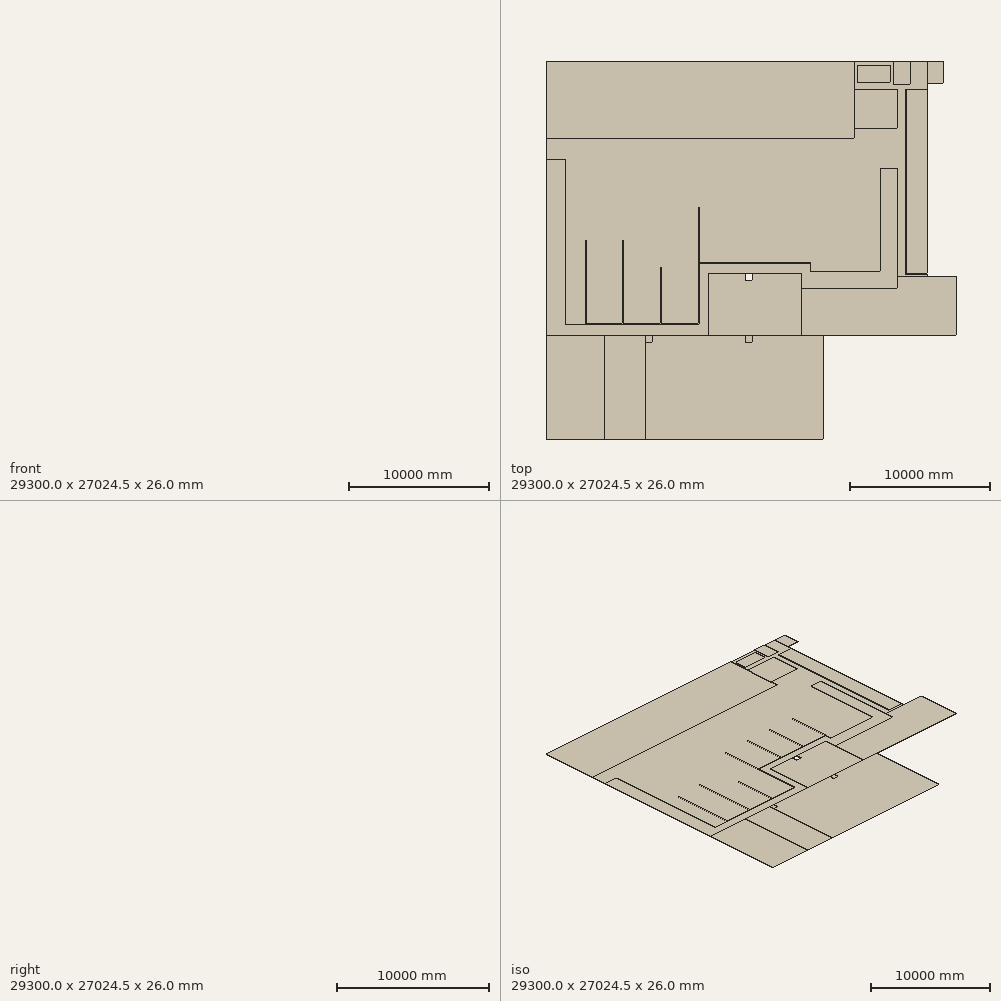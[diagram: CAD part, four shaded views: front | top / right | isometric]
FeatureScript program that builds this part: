
annotation { "Feature Type Name" : "Feature", "Feature Type Description" : "" }
export const myFeature = defineFeature(function(context is Context, id is Id, definition is map)
    precondition{}
    {
        {
            var Q0;
            Q0=qCreatedBy(makeId("Top.planeOp"),FACE);
            var sketch = newSketch(context, id + "F0", { "sketchPlane" : qUnion([Q0])});
            skLineSegment(sketch, "E0", {"start": v(10928.58, -1480) * mm, "end": v(12438.58, -1480) * mm});
            skLineSegment(sketch, "E1", {"start": v(12438.58, 11730) * mm, "end": v(10928.58, 11730) * mm});
            skLineSegment(sketch, "E2", {"start": v(10928.58, 11730) * mm, "end": v(10928.58, -1480) * mm});
            skLineSegment(sketch, "E3", {"start": v(10938.58, 11720) * mm, "end": v(10938.58, -1470) * mm});
            skLineSegment(sketch, "E4", {"start": v(12438.58, 11720) * mm, "end": v(10938.58, 11720) * mm});
            skLineSegment(sketch, "E5", {"start": v(10938.58, -1470) * mm, "end": v(12438.58, -1470) * mm});
            skLineSegment(sketch, "E6", {"start": v(12438.58, -1470) * mm, "end": v(12438.58, -1480) * mm});
            skLineSegment(sketch, "E7", {"start": v(12438.58, 11730) * mm, "end": v(12438.58, 11720) * mm});
            skLineSegment(sketch, "E8", {"start": v(13638.58, 12120) * mm, "end": v(13638.58, 13720) * mm});
            skLineSegment(sketch, "E9", {"start": v(12438.58, 12120) * mm, "end": v(13638.58, 12120) * mm});
            skLineSegment(sketch, "E10", {"start": v(12438.58, 11730) * mm, "end": v(12438.58, 12120) * mm});
            skLineSegment(sketch, "E11", {"start": v(-14761.42, -5870) * mm, "end": v(-14761.42, -13304.54) * mm});
            skLineSegment(sketch, "E12", {"start": v(-14761.42, -13304.54) * mm, "end": v(5038.58, -13304.54) * mm});
            skLineSegment(sketch, "E13", {"start": v(5038.58, -13304.54) * mm, "end": v(5038.58, -5870) * mm});
            skLineSegment(sketch, "E14", {"start": v(12438.58, -1670) * mm, "end": v(14538.58, -1670) * mm});
            skLineSegment(sketch, "E15", {"start": v(14538.58, -1670) * mm, "end": v(14538.58, -5870) * mm});
            skLineSegment(sketch, "E16", {"start": v(14538.58, -5870) * mm, "end": v(5038.58, -5870) * mm});
            skLineSegment(sketch, "E17", {"start": v(12438.58, -1480) * mm, "end": v(12438.58, -1670) * mm});
            skLineSegment(sketch, "E18", {"start": v(13638.58, 13720) * mm, "end": v(13542.58, 13720) * mm});
            skLineSegment(sketch, "E19", {"start": v(13542.58, 13720) * mm, "end": v(13540.58, 13718) * mm});
            skLineSegment(sketch, "E20", {"start": v(13540.58, 13718) * mm, "end": v(13440.58, 13718) * mm});
            skLineSegment(sketch, "E21", {"start": v(13440.58, 13718) * mm, "end": v(13438.58, 13720) * mm});
            skLineSegment(sketch, "E22", {"start": v(13438.58, 13720) * mm, "end": v(13142.58, 13720) * mm});
            skLineSegment(sketch, "E23", {"start": v(13142.58, 13720) * mm, "end": v(13140.58, 13718) * mm});
            skLineSegment(sketch, "E24", {"start": v(13140.58, 13718) * mm, "end": v(13040.58, 13718) * mm});
            skLineSegment(sketch, "E25", {"start": v(13040.58, 13718) * mm, "end": v(13038.58, 13720) * mm});
            skLineSegment(sketch, "E26", {"start": v(13038.58, 13720) * mm, "end": v(12742.58, 13720) * mm});
            skLineSegment(sketch, "E27", {"start": v(12742.58, 13720) * mm, "end": v(12740.58, 13718) * mm});
            skLineSegment(sketch, "E28", {"start": v(12740.58, 13718) * mm, "end": v(12640.58, 13718) * mm});
            skLineSegment(sketch, "E29", {"start": v(12640.58, 13718) * mm, "end": v(12638.58, 13720) * mm});
            skLineSegment(sketch, "E30", {"start": v(12638.58, 13720) * mm, "end": v(12342.58, 13720) * mm});
            skLineSegment(sketch, "E31", {"start": v(12342.58, 13720) * mm, "end": v(12340.58, 13718) * mm});
            skLineSegment(sketch, "E32", {"start": v(12340.58, 13718) * mm, "end": v(12240.58, 13718) * mm});
            skLineSegment(sketch, "E33", {"start": v(12240.58, 13718) * mm, "end": v(12238.58, 13720) * mm});
            skLineSegment(sketch, "E34", {"start": v(12238.58, 13720) * mm, "end": v(11942.58, 13720) * mm});
            skLineSegment(sketch, "E35", {"start": v(11942.58, 13720) * mm, "end": v(11940.58, 13718) * mm});
            skLineSegment(sketch, "E36", {"start": v(11940.58, 13718) * mm, "end": v(11840.58, 13718) * mm});
            skLineSegment(sketch, "E37", {"start": v(11840.58, 13718) * mm, "end": v(11838.58, 13720) * mm});
            skLineSegment(sketch, "E38", {"start": v(11838.58, 13720) * mm, "end": v(11542.58, 13720) * mm});
            skLineSegment(sketch, "E39", {"start": v(11542.58, 13720) * mm, "end": v(11540.58, 13718) * mm});
            skLineSegment(sketch, "E40", {"start": v(11540.58, 13718) * mm, "end": v(11440.58, 13718) * mm});
            skLineSegment(sketch, "E41", {"start": v(11440.58, 13718) * mm, "end": v(11438.58, 13720) * mm});
            skLineSegment(sketch, "E42", {"start": v(11438.58, 13720) * mm, "end": v(11142.58, 13720) * mm});
            skLineSegment(sketch, "E43", {"start": v(11142.58, 13720) * mm, "end": v(11140.58, 13718) * mm});
            skLineSegment(sketch, "E44", {"start": v(11140.58, 13718) * mm, "end": v(11040.58, 13718) * mm});
            skLineSegment(sketch, "E45", {"start": v(11040.58, 13718) * mm, "end": v(11038.58, 13720) * mm});
            skLineSegment(sketch, "E46", {"start": v(11038.58, 13720) * mm, "end": v(10742.58, 13720) * mm});
            skLineSegment(sketch, "E47", {"start": v(10742.58, 13720) * mm, "end": v(10740.58, 13718) * mm});
            skLineSegment(sketch, "E48", {"start": v(10740.58, 13718) * mm, "end": v(10640.58, 13718) * mm});
            skLineSegment(sketch, "E49", {"start": v(10640.58, 13718) * mm, "end": v(10638.58, 13720) * mm});
            skLineSegment(sketch, "E50", {"start": v(10638.58, 13720) * mm, "end": v(10342.58, 13720) * mm});
            skLineSegment(sketch, "E51", {"start": v(10342.58, 13720) * mm, "end": v(10340.58, 13718) * mm});
            skLineSegment(sketch, "E52", {"start": v(10340.58, 13718) * mm, "end": v(10240.58, 13718) * mm});
            skLineSegment(sketch, "E53", {"start": v(10240.58, 13718) * mm, "end": v(10238.58, 13720) * mm});
            skLineSegment(sketch, "E54", {"start": v(10238.58, 13720) * mm, "end": v(9942.58, 13720) * mm});
            skLineSegment(sketch, "E55", {"start": v(9942.58, 13720) * mm, "end": v(9940.58, 13718) * mm});
            skLineSegment(sketch, "E56", {"start": v(9940.58, 13718) * mm, "end": v(9840.58, 13718) * mm});
            skLineSegment(sketch, "E57", {"start": v(9840.58, 13718) * mm, "end": v(9838.58, 13720) * mm});
            skLineSegment(sketch, "E58", {"start": v(9838.58, 13720) * mm, "end": v(9542.58, 13720) * mm});
            skLineSegment(sketch, "E59", {"start": v(9542.58, 13720) * mm, "end": v(9540.58, 13718) * mm});
            skLineSegment(sketch, "E60", {"start": v(9540.58, 13718) * mm, "end": v(9440.58, 13718) * mm});
            skLineSegment(sketch, "E61", {"start": v(9440.58, 13718) * mm, "end": v(9438.58, 13720) * mm});
            skLineSegment(sketch, "E62", {"start": v(9438.58, 13720) * mm, "end": v(9142.58, 13720) * mm});
            skLineSegment(sketch, "E63", {"start": v(9142.58, 13720) * mm, "end": v(9140.58, 13718) * mm});
            skLineSegment(sketch, "E64", {"start": v(9140.58, 13718) * mm, "end": v(9040.58, 13718) * mm});
            skLineSegment(sketch, "E65", {"start": v(9040.58, 13718) * mm, "end": v(9038.58, 13720) * mm});
            skLineSegment(sketch, "E66", {"start": v(9038.58, 13720) * mm, "end": v(8742.58, 13720) * mm});
            skLineSegment(sketch, "E67", {"start": v(8742.58, 13720) * mm, "end": v(8740.58, 13718) * mm});
            skLineSegment(sketch, "E68", {"start": v(8740.58, 13718) * mm, "end": v(8640.58, 13718) * mm});
            skLineSegment(sketch, "E69", {"start": v(8640.58, 13718) * mm, "end": v(8638.58, 13720) * mm});
            skLineSegment(sketch, "E70", {"start": v(8638.58, 13720) * mm, "end": v(8342.58, 13720) * mm});
            skLineSegment(sketch, "E71", {"start": v(8342.58, 13720) * mm, "end": v(8340.58, 13718) * mm});
            skLineSegment(sketch, "E72", {"start": v(8340.58, 13718) * mm, "end": v(8240.58, 13718) * mm});
            skLineSegment(sketch, "E73", {"start": v(8240.58, 13718) * mm, "end": v(8238.58, 13720) * mm});
            skLineSegment(sketch, "E74", {"start": v(8238.58, 13720) * mm, "end": v(7942.58, 13720) * mm});
            skLineSegment(sketch, "E75", {"start": v(7942.58, 13720) * mm, "end": v(7940.58, 13718) * mm});
            skLineSegment(sketch, "E76", {"start": v(7940.58, 13718) * mm, "end": v(7840.58, 13718) * mm});
            skLineSegment(sketch, "E77", {"start": v(7840.58, 13718) * mm, "end": v(7838.58, 13720) * mm});
            skLineSegment(sketch, "E78", {"start": v(7838.58, 13720) * mm, "end": v(7542.58, 13720) * mm});
            skLineSegment(sketch, "E79", {"start": v(7542.58, 13720) * mm, "end": v(7540.58, 13718) * mm});
            skLineSegment(sketch, "E80", {"start": v(7540.58, 13718) * mm, "end": v(7440.58, 13718) * mm});
            skLineSegment(sketch, "E81", {"start": v(7440.58, 13718) * mm, "end": v(7438.58, 13720) * mm});
            skLineSegment(sketch, "E82", {"start": v(7438.58, 13720) * mm, "end": v(7142.58, 13720) * mm});
            skLineSegment(sketch, "E83", {"start": v(7142.58, 13720) * mm, "end": v(7140.58, 13718) * mm});
            skLineSegment(sketch, "E84", {"start": v(7140.58, 13718) * mm, "end": v(7040.58, 13718) * mm});
            skLineSegment(sketch, "E85", {"start": v(7040.58, 13718) * mm, "end": v(7038.58, 13720) * mm});
            skLineSegment(sketch, "E86", {"start": v(7038.58, 13720) * mm, "end": v(6742.58, 13720) * mm});
            skLineSegment(sketch, "E87", {"start": v(6742.58, 13720) * mm, "end": v(6740.58, 13718) * mm});
            skLineSegment(sketch, "E88", {"start": v(6740.58, 13718) * mm, "end": v(6640.58, 13718) * mm});
            skLineSegment(sketch, "E89", {"start": v(6640.58, 13718) * mm, "end": v(6638.58, 13720) * mm});
            skLineSegment(sketch, "E90", {"start": v(6638.58, 13720) * mm, "end": v(6342.58, 13720) * mm});
            skLineSegment(sketch, "E91", {"start": v(6342.58, 13720) * mm, "end": v(6340.58, 13718) * mm});
            skLineSegment(sketch, "E92", {"start": v(6340.58, 13718) * mm, "end": v(6240.58, 13718) * mm});
            skLineSegment(sketch, "E93", {"start": v(6240.58, 13718) * mm, "end": v(6238.58, 13720) * mm});
            skLineSegment(sketch, "E94", {"start": v(6238.58, 13720) * mm, "end": v(5942.58, 13720) * mm});
            skLineSegment(sketch, "E95", {"start": v(5942.58, 13720) * mm, "end": v(5940.58, 13718) * mm});
            skLineSegment(sketch, "E96", {"start": v(5940.58, 13718) * mm, "end": v(5840.58, 13718) * mm});
            skLineSegment(sketch, "E97", {"start": v(5840.58, 13718) * mm, "end": v(5838.58, 13720) * mm});
            skLineSegment(sketch, "E98", {"start": v(5838.58, 13720) * mm, "end": v(5542.58, 13720) * mm});
            skLineSegment(sketch, "E99", {"start": v(5542.58, 13720) * mm, "end": v(5540.58, 13718) * mm});
            skLineSegment(sketch, "E100", {"start": v(5540.58, 13718) * mm, "end": v(5440.58, 13718) * mm});
            skLineSegment(sketch, "E101", {"start": v(5440.58, 13718) * mm, "end": v(5438.58, 13720) * mm});
            skLineSegment(sketch, "E102", {"start": v(5438.58, 13720) * mm, "end": v(5142.58, 13720) * mm});
            skLineSegment(sketch, "E103", {"start": v(5142.58, 13720) * mm, "end": v(5140.58, 13718) * mm});
            skLineSegment(sketch, "E104", {"start": v(5140.58, 13718) * mm, "end": v(5040.58, 13718) * mm});
            skLineSegment(sketch, "E105", {"start": v(5040.58, 13718) * mm, "end": v(5038.58, 13720) * mm});
            skLineSegment(sketch, "E106", {"start": v(5038.58, 13720) * mm, "end": v(4742.58, 13720) * mm});
            skLineSegment(sketch, "E107", {"start": v(4742.58, 13720) * mm, "end": v(4740.58, 13718) * mm});
            skLineSegment(sketch, "E108", {"start": v(4740.58, 13718) * mm, "end": v(4640.58, 13718) * mm});
            skLineSegment(sketch, "E109", {"start": v(4640.58, 13718) * mm, "end": v(4638.58, 13720) * mm});
            skLineSegment(sketch, "E110", {"start": v(4638.58, 13720) * mm, "end": v(4342.58, 13720) * mm});
            skLineSegment(sketch, "E111", {"start": v(4342.58, 13720) * mm, "end": v(4340.58, 13718) * mm});
            skLineSegment(sketch, "E112", {"start": v(4340.58, 13718) * mm, "end": v(4240.58, 13718) * mm});
            skLineSegment(sketch, "E113", {"start": v(4240.58, 13718) * mm, "end": v(4238.58, 13720) * mm});
            skLineSegment(sketch, "E114", {"start": v(4238.58, 13720) * mm, "end": v(3942.58, 13720) * mm});
            skLineSegment(sketch, "E115", {"start": v(3942.58, 13720) * mm, "end": v(3940.58, 13718) * mm});
            skLineSegment(sketch, "E116", {"start": v(3940.58, 13718) * mm, "end": v(3840.58, 13718) * mm});
            skLineSegment(sketch, "E117", {"start": v(3840.58, 13718) * mm, "end": v(3838.58, 13720) * mm});
            skLineSegment(sketch, "E118", {"start": v(3838.58, 13720) * mm, "end": v(3542.58, 13720) * mm});
            skLineSegment(sketch, "E119", {"start": v(3542.58, 13720) * mm, "end": v(3540.58, 13718) * mm});
            skLineSegment(sketch, "E120", {"start": v(3540.58, 13718) * mm, "end": v(3440.58, 13718) * mm});
            skLineSegment(sketch, "E121", {"start": v(3440.58, 13718) * mm, "end": v(3438.58, 13720) * mm});
            skLineSegment(sketch, "E122", {"start": v(3438.58, 13720) * mm, "end": v(3142.58, 13720) * mm});
            skLineSegment(sketch, "E123", {"start": v(3142.58, 13720) * mm, "end": v(3140.58, 13718) * mm});
            skLineSegment(sketch, "E124", {"start": v(3140.58, 13718) * mm, "end": v(3040.58, 13718) * mm});
            skLineSegment(sketch, "E125", {"start": v(3040.58, 13718) * mm, "end": v(3038.58, 13720) * mm});
            skLineSegment(sketch, "E126", {"start": v(3038.58, 13720) * mm, "end": v(2742.58, 13720) * mm});
            skLineSegment(sketch, "E127", {"start": v(2742.58, 13720) * mm, "end": v(2740.58, 13718) * mm});
            skLineSegment(sketch, "E128", {"start": v(2740.58, 13718) * mm, "end": v(2640.58, 13718) * mm});
            skLineSegment(sketch, "E129", {"start": v(2640.58, 13718) * mm, "end": v(2638.58, 13720) * mm});
            skLineSegment(sketch, "E130", {"start": v(2638.58, 13720) * mm, "end": v(2342.58, 13720) * mm});
            skLineSegment(sketch, "E131", {"start": v(2342.58, 13720) * mm, "end": v(2340.58, 13718) * mm});
            skLineSegment(sketch, "E132", {"start": v(2340.58, 13718) * mm, "end": v(2240.58, 13718) * mm});
            skLineSegment(sketch, "E133", {"start": v(2240.58, 13718) * mm, "end": v(2238.58, 13720) * mm});
            skLineSegment(sketch, "E134", {"start": v(2238.58, 13720) * mm, "end": v(1942.58, 13720) * mm});
            skLineSegment(sketch, "E135", {"start": v(1942.58, 13720) * mm, "end": v(1940.58, 13718) * mm});
            skLineSegment(sketch, "E136", {"start": v(1940.58, 13718) * mm, "end": v(1840.58, 13718) * mm});
            skLineSegment(sketch, "E137", {"start": v(1840.58, 13718) * mm, "end": v(1838.58, 13720) * mm});
            skLineSegment(sketch, "E138", {"start": v(1838.58, 13720) * mm, "end": v(1542.58, 13720) * mm});
            skLineSegment(sketch, "E139", {"start": v(1542.58, 13720) * mm, "end": v(1540.58, 13718) * mm});
            skLineSegment(sketch, "E140", {"start": v(1540.58, 13718) * mm, "end": v(1440.58, 13718) * mm});
            skLineSegment(sketch, "E141", {"start": v(1440.58, 13718) * mm, "end": v(1438.58, 13720) * mm});
            skLineSegment(sketch, "E142", {"start": v(1438.58, 13720) * mm, "end": v(1142.58, 13720) * mm});
            skLineSegment(sketch, "E143", {"start": v(1142.58, 13720) * mm, "end": v(1140.58, 13718) * mm});
            skLineSegment(sketch, "E144", {"start": v(1140.58, 13718) * mm, "end": v(1040.58, 13718) * mm});
            skLineSegment(sketch, "E145", {"start": v(1040.58, 13718) * mm, "end": v(1038.58, 13720) * mm});
            skLineSegment(sketch, "E146", {"start": v(1038.58, 13720) * mm, "end": v(742.58, 13720) * mm});
            skLineSegment(sketch, "E147", {"start": v(742.58, 13720) * mm, "end": v(740.58, 13718) * mm});
            skLineSegment(sketch, "E148", {"start": v(740.58, 13718) * mm, "end": v(640.58, 13718) * mm});
            skLineSegment(sketch, "E149", {"start": v(640.58, 13718) * mm, "end": v(638.58, 13720) * mm});
            skLineSegment(sketch, "E150", {"start": v(638.58, 13720) * mm, "end": v(342.58, 13720) * mm});
            skLineSegment(sketch, "E151", {"start": v(342.58, 13720) * mm, "end": v(340.58, 13718) * mm});
            skLineSegment(sketch, "E152", {"start": v(340.58, 13718) * mm, "end": v(240.58, 13718) * mm});
            skLineSegment(sketch, "E153", {"start": v(240.58, 13718) * mm, "end": v(238.58, 13720) * mm});
            skLineSegment(sketch, "E154", {"start": v(238.58, 13720) * mm, "end": v(-57.42, 13720) * mm});
            skLineSegment(sketch, "E155", {"start": v(-57.42, 13720) * mm, "end": v(-59.42, 13718) * mm});
            skLineSegment(sketch, "E156", {"start": v(-59.42, 13718) * mm, "end": v(-159.42, 13718) * mm});
            skLineSegment(sketch, "E157", {"start": v(-159.42, 13718) * mm, "end": v(-161.42, 13720) * mm});
            skLineSegment(sketch, "E158", {"start": v(-161.42, 13720) * mm, "end": v(-457.42, 13720) * mm});
            skLineSegment(sketch, "E159", {"start": v(-457.42, 13720) * mm, "end": v(-459.42, 13718) * mm});
            skLineSegment(sketch, "E160", {"start": v(-459.42, 13718) * mm, "end": v(-559.42, 13718) * mm});
            skLineSegment(sketch, "E161", {"start": v(-559.42, 13718) * mm, "end": v(-561.42, 13720) * mm});
            skLineSegment(sketch, "E162", {"start": v(-561.42, 13720) * mm, "end": v(-857.42, 13720) * mm});
            skLineSegment(sketch, "E163", {"start": v(-857.42, 13720) * mm, "end": v(-859.42, 13718) * mm});
            skLineSegment(sketch, "E164", {"start": v(-859.42, 13718) * mm, "end": v(-959.42, 13718) * mm});
            skLineSegment(sketch, "E165", {"start": v(-959.42, 13718) * mm, "end": v(-961.42, 13720) * mm});
            skLineSegment(sketch, "E166", {"start": v(-961.42, 13720) * mm, "end": v(-1257.42, 13720) * mm});
            skLineSegment(sketch, "E167", {"start": v(-1257.42, 13720) * mm, "end": v(-1259.42, 13718) * mm});
            skLineSegment(sketch, "E168", {"start": v(-1259.42, 13718) * mm, "end": v(-1359.42, 13718) * mm});
            skLineSegment(sketch, "E169", {"start": v(-1359.42, 13718) * mm, "end": v(-1361.42, 13720) * mm});
            skLineSegment(sketch, "E170", {"start": v(-1361.42, 13720) * mm, "end": v(-1657.42, 13720) * mm});
            skLineSegment(sketch, "E171", {"start": v(-1657.42, 13720) * mm, "end": v(-1659.42, 13718) * mm});
            skLineSegment(sketch, "E172", {"start": v(-1659.42, 13718) * mm, "end": v(-1759.42, 13718) * mm});
            skLineSegment(sketch, "E173", {"start": v(-1759.42, 13718) * mm, "end": v(-1761.42, 13720) * mm});
            skLineSegment(sketch, "E174", {"start": v(-1761.42, 13720) * mm, "end": v(-2057.42, 13720) * mm});
            skLineSegment(sketch, "E175", {"start": v(-2057.42, 13720) * mm, "end": v(-2059.42, 13718) * mm});
            skLineSegment(sketch, "E176", {"start": v(-2059.42, 13718) * mm, "end": v(-2159.42, 13718) * mm});
            skLineSegment(sketch, "E177", {"start": v(-2159.42, 13718) * mm, "end": v(-2161.42, 13720) * mm});
            skLineSegment(sketch, "E178", {"start": v(-2161.42, 13720) * mm, "end": v(-2457.42, 13720) * mm});
            skLineSegment(sketch, "E179", {"start": v(-2457.42, 13720) * mm, "end": v(-2459.42, 13718) * mm});
            skLineSegment(sketch, "E180", {"start": v(-2459.42, 13718) * mm, "end": v(-2559.42, 13718) * mm});
            skLineSegment(sketch, "E181", {"start": v(-2559.42, 13718) * mm, "end": v(-2561.42, 13720) * mm});
            skLineSegment(sketch, "E182", {"start": v(-2561.42, 13720) * mm, "end": v(-2857.42, 13720) * mm});
            skLineSegment(sketch, "E183", {"start": v(-2857.42, 13720) * mm, "end": v(-2859.42, 13718) * mm});
            skLineSegment(sketch, "E184", {"start": v(-2859.42, 13718) * mm, "end": v(-2959.42, 13718) * mm});
            skLineSegment(sketch, "E185", {"start": v(-2959.42, 13718) * mm, "end": v(-2961.42, 13720) * mm});
            skLineSegment(sketch, "E186", {"start": v(-2961.42, 13720) * mm, "end": v(-3257.42, 13720) * mm});
            skLineSegment(sketch, "E187", {"start": v(-3257.42, 13720) * mm, "end": v(-3259.42, 13718) * mm});
            skLineSegment(sketch, "E188", {"start": v(-3259.42, 13718) * mm, "end": v(-3359.42, 13718) * mm});
            skLineSegment(sketch, "E189", {"start": v(-3359.42, 13718) * mm, "end": v(-3361.42, 13720) * mm});
            skLineSegment(sketch, "E190", {"start": v(-3361.42, 13720) * mm, "end": v(-3657.42, 13720) * mm});
            skLineSegment(sketch, "E191", {"start": v(-3657.42, 13720) * mm, "end": v(-3659.42, 13718) * mm});
            skLineSegment(sketch, "E192", {"start": v(-3659.42, 13718) * mm, "end": v(-3759.42, 13718) * mm});
            skLineSegment(sketch, "E193", {"start": v(-3759.42, 13718) * mm, "end": v(-3761.42, 13720) * mm});
            skLineSegment(sketch, "E194", {"start": v(-3761.42, 13720) * mm, "end": v(-4057.42, 13720) * mm});
            skLineSegment(sketch, "E195", {"start": v(-4057.42, 13720) * mm, "end": v(-4059.42, 13718) * mm});
            skLineSegment(sketch, "E196", {"start": v(-4059.42, 13718) * mm, "end": v(-4159.42, 13718) * mm});
            skLineSegment(sketch, "E197", {"start": v(-4159.42, 13718) * mm, "end": v(-4161.42, 13720) * mm});
            skLineSegment(sketch, "E198", {"start": v(-4161.42, 13720) * mm, "end": v(-4457.42, 13720) * mm});
            skLineSegment(sketch, "E199", {"start": v(-4457.42, 13720) * mm, "end": v(-4459.42, 13718) * mm});
            skLineSegment(sketch, "E200", {"start": v(-4459.42, 13718) * mm, "end": v(-4559.42, 13718) * mm});
            skLineSegment(sketch, "E201", {"start": v(-4559.42, 13718) * mm, "end": v(-4561.42, 13720) * mm});
            skLineSegment(sketch, "E202", {"start": v(-4561.42, 13720) * mm, "end": v(-4857.42, 13720) * mm});
            skLineSegment(sketch, "E203", {"start": v(-4857.42, 13720) * mm, "end": v(-4859.42, 13718) * mm});
            skLineSegment(sketch, "E204", {"start": v(-4859.42, 13718) * mm, "end": v(-4959.42, 13718) * mm});
            skLineSegment(sketch, "E205", {"start": v(-4959.42, 13718) * mm, "end": v(-4961.42, 13720) * mm});
            skLineSegment(sketch, "E206", {"start": v(-4961.42, 13720) * mm, "end": v(-5257.42, 13720) * mm});
            skLineSegment(sketch, "E207", {"start": v(-5257.42, 13720) * mm, "end": v(-5259.42, 13718) * mm});
            skLineSegment(sketch, "E208", {"start": v(-5259.42, 13718) * mm, "end": v(-5359.42, 13718) * mm});
            skLineSegment(sketch, "E209", {"start": v(-5359.42, 13718) * mm, "end": v(-5361.42, 13720) * mm});
            skLineSegment(sketch, "E210", {"start": v(-5361.42, 13720) * mm, "end": v(-5657.42, 13720) * mm});
            skLineSegment(sketch, "E211", {"start": v(-5657.42, 13720) * mm, "end": v(-5659.42, 13718) * mm});
            skLineSegment(sketch, "E212", {"start": v(-5659.42, 13718) * mm, "end": v(-5759.42, 13718) * mm});
            skLineSegment(sketch, "E213", {"start": v(-5759.42, 13718) * mm, "end": v(-5761.42, 13720) * mm});
            skLineSegment(sketch, "E214", {"start": v(-5761.42, 13720) * mm, "end": v(-6057.42, 13720) * mm});
            skLineSegment(sketch, "E215", {"start": v(-6057.42, 13720) * mm, "end": v(-6059.42, 13718) * mm});
            skLineSegment(sketch, "E216", {"start": v(-6059.42, 13718) * mm, "end": v(-6159.42, 13718) * mm});
            skLineSegment(sketch, "E217", {"start": v(-6159.42, 13718) * mm, "end": v(-6161.42, 13720) * mm});
            skLineSegment(sketch, "E218", {"start": v(-6161.42, 13720) * mm, "end": v(-6457.42, 13720) * mm});
            skLineSegment(sketch, "E219", {"start": v(-6457.42, 13720) * mm, "end": v(-6459.42, 13718) * mm});
            skLineSegment(sketch, "E220", {"start": v(-6459.42, 13718) * mm, "end": v(-6559.42, 13718) * mm});
            skLineSegment(sketch, "E221", {"start": v(-6559.42, 13718) * mm, "end": v(-6561.42, 13720) * mm});
            skLineSegment(sketch, "E222", {"start": v(-6561.42, 13720) * mm, "end": v(-6857.42, 13720) * mm});
            skLineSegment(sketch, "E223", {"start": v(-6857.42, 13720) * mm, "end": v(-6859.42, 13718) * mm});
            skLineSegment(sketch, "E224", {"start": v(-6859.42, 13718) * mm, "end": v(-6959.42, 13718) * mm});
            skLineSegment(sketch, "E225", {"start": v(-6959.42, 13718) * mm, "end": v(-6961.42, 13720) * mm});
            skLineSegment(sketch, "E226", {"start": v(-6961.42, 13720) * mm, "end": v(-7257.42, 13720) * mm});
            skLineSegment(sketch, "E227", {"start": v(-7257.42, 13720) * mm, "end": v(-7259.42, 13718) * mm});
            skLineSegment(sketch, "E228", {"start": v(-7259.42, 13718) * mm, "end": v(-7359.42, 13718) * mm});
            skLineSegment(sketch, "E229", {"start": v(-7359.42, 13718) * mm, "end": v(-7361.42, 13720) * mm});
            skLineSegment(sketch, "E230", {"start": v(-7361.42, 13720) * mm, "end": v(-7657.42, 13720) * mm});
            skLineSegment(sketch, "E231", {"start": v(-7657.42, 13720) * mm, "end": v(-7659.42, 13718) * mm});
            skLineSegment(sketch, "E232", {"start": v(-7659.42, 13718) * mm, "end": v(-7759.42, 13718) * mm});
            skLineSegment(sketch, "E233", {"start": v(-7759.42, 13718) * mm, "end": v(-7761.42, 13720) * mm});
            skLineSegment(sketch, "E234", {"start": v(-7761.42, 13720) * mm, "end": v(-8057.42, 13720) * mm});
            skLineSegment(sketch, "E235", {"start": v(-8057.42, 13720) * mm, "end": v(-8059.42, 13718) * mm});
            skLineSegment(sketch, "E236", {"start": v(-8059.42, 13718) * mm, "end": v(-8159.42, 13718) * mm});
            skLineSegment(sketch, "E237", {"start": v(-8159.42, 13718) * mm, "end": v(-8161.42, 13720) * mm});
            skLineSegment(sketch, "E238", {"start": v(-8161.42, 13720) * mm, "end": v(-8457.42, 13720) * mm});
            skLineSegment(sketch, "E239", {"start": v(-8457.42, 13720) * mm, "end": v(-8459.42, 13718) * mm});
            skLineSegment(sketch, "E240", {"start": v(-8459.42, 13718) * mm, "end": v(-8559.42, 13718) * mm});
            skLineSegment(sketch, "E241", {"start": v(-8559.42, 13718) * mm, "end": v(-8561.42, 13720) * mm});
            skLineSegment(sketch, "E242", {"start": v(-8561.42, 13720) * mm, "end": v(-8857.42, 13720) * mm});
            skLineSegment(sketch, "E243", {"start": v(-8857.42, 13720) * mm, "end": v(-8859.42, 13718) * mm});
            skLineSegment(sketch, "E244", {"start": v(-8859.42, 13718) * mm, "end": v(-8959.42, 13718) * mm});
            skLineSegment(sketch, "E245", {"start": v(-8959.42, 13718) * mm, "end": v(-8961.42, 13720) * mm});
            skLineSegment(sketch, "E246", {"start": v(-8961.42, 13720) * mm, "end": v(-9257.42, 13720) * mm});
            skLineSegment(sketch, "E247", {"start": v(-9257.42, 13720) * mm, "end": v(-9259.42, 13718) * mm});
            skLineSegment(sketch, "E248", {"start": v(-9259.42, 13718) * mm, "end": v(-9359.42, 13718) * mm});
            skLineSegment(sketch, "E249", {"start": v(-9359.42, 13718) * mm, "end": v(-9361.42, 13720) * mm});
            skLineSegment(sketch, "E250", {"start": v(-9361.42, 13720) * mm, "end": v(-9657.42, 13720) * mm});
            skLineSegment(sketch, "E251", {"start": v(-9657.42, 13720) * mm, "end": v(-9659.42, 13718) * mm});
            skLineSegment(sketch, "E252", {"start": v(-9659.42, 13718) * mm, "end": v(-9759.42, 13718) * mm});
            skLineSegment(sketch, "E253", {"start": v(-9759.42, 13718) * mm, "end": v(-9761.42, 13720) * mm});
            skLineSegment(sketch, "E254", {"start": v(-9761.42, 13720) * mm, "end": v(-10057.42, 13720) * mm});
            skLineSegment(sketch, "E255", {"start": v(-10057.42, 13720) * mm, "end": v(-10059.42, 13718) * mm});
            skLineSegment(sketch, "E256", {"start": v(-10059.42, 13718) * mm, "end": v(-10159.42, 13718) * mm});
            skLineSegment(sketch, "E257", {"start": v(-10159.42, 13718) * mm, "end": v(-10161.42, 13720) * mm});
            skLineSegment(sketch, "E258", {"start": v(-10161.42, 13720) * mm, "end": v(-10457.42, 13720) * mm});
            skLineSegment(sketch, "E259", {"start": v(-10457.42, 13720) * mm, "end": v(-10459.42, 13718) * mm});
            skLineSegment(sketch, "E260", {"start": v(-10459.42, 13718) * mm, "end": v(-10559.42, 13718) * mm});
            skLineSegment(sketch, "E261", {"start": v(-10559.42, 13718) * mm, "end": v(-10561.42, 13720) * mm});
            skLineSegment(sketch, "E262", {"start": v(-10561.42, 13720) * mm, "end": v(-10857.42, 13720) * mm});
            skLineSegment(sketch, "E263", {"start": v(-10857.42, 13720) * mm, "end": v(-10859.42, 13718) * mm});
            skLineSegment(sketch, "E264", {"start": v(-10859.42, 13718) * mm, "end": v(-10959.42, 13718) * mm});
            skLineSegment(sketch, "E265", {"start": v(-10959.42, 13718) * mm, "end": v(-10961.42, 13720) * mm});
            skLineSegment(sketch, "E266", {"start": v(-10961.42, 13720) * mm, "end": v(-11257.42, 13720) * mm});
            skLineSegment(sketch, "E267", {"start": v(-11257.42, 13720) * mm, "end": v(-11259.42, 13718) * mm});
            skLineSegment(sketch, "E268", {"start": v(-11259.42, 13718) * mm, "end": v(-11359.42, 13718) * mm});
            skLineSegment(sketch, "E269", {"start": v(-11359.42, 13718) * mm, "end": v(-11361.42, 13720) * mm});
            skLineSegment(sketch, "E270", {"start": v(-11361.42, 13720) * mm, "end": v(-11657.42, 13720) * mm});
            skLineSegment(sketch, "E271", {"start": v(-11657.42, 13720) * mm, "end": v(-11659.42, 13718) * mm});
            skLineSegment(sketch, "E272", {"start": v(-11659.42, 13718) * mm, "end": v(-11759.42, 13718) * mm});
            skLineSegment(sketch, "E273", {"start": v(-11759.42, 13718) * mm, "end": v(-11761.42, 13720) * mm});
            skLineSegment(sketch, "E274", {"start": v(-11761.42, 13720) * mm, "end": v(-12057.42, 13720) * mm});
            skLineSegment(sketch, "E275", {"start": v(-12057.42, 13720) * mm, "end": v(-12059.42, 13718) * mm});
            skLineSegment(sketch, "E276", {"start": v(-12059.42, 13718) * mm, "end": v(-12159.42, 13718) * mm});
            skLineSegment(sketch, "E277", {"start": v(-12159.42, 13718) * mm, "end": v(-12161.42, 13720) * mm});
            skLineSegment(sketch, "E278", {"start": v(-12161.42, 13720) * mm, "end": v(-12457.42, 13720) * mm});
            skLineSegment(sketch, "E279", {"start": v(-12457.42, 13720) * mm, "end": v(-12459.42, 13718) * mm});
            skLineSegment(sketch, "E280", {"start": v(-12459.42, 13718) * mm, "end": v(-12559.42, 13718) * mm});
            skLineSegment(sketch, "E281", {"start": v(-12559.42, 13718) * mm, "end": v(-12561.42, 13720) * mm});
            skLineSegment(sketch, "E282", {"start": v(-12561.42, 13720) * mm, "end": v(-12857.42, 13720) * mm});
            skLineSegment(sketch, "E283", {"start": v(-12857.42, 13720) * mm, "end": v(-12859.42, 13718) * mm});
            skLineSegment(sketch, "E284", {"start": v(-12859.42, 13718) * mm, "end": v(-12959.42, 13718) * mm});
            skLineSegment(sketch, "E285", {"start": v(-12959.42, 13718) * mm, "end": v(-12961.42, 13720) * mm});
            skLineSegment(sketch, "E286", {"start": v(-12961.42, 13720) * mm, "end": v(-13257.42, 13720) * mm});
            skLineSegment(sketch, "E287", {"start": v(-13257.42, 13720) * mm, "end": v(-13259.42, 13718) * mm});
            skLineSegment(sketch, "E288", {"start": v(-13259.42, 13718) * mm, "end": v(-13359.42, 13718) * mm});
            skLineSegment(sketch, "E289", {"start": v(-13359.42, 13718) * mm, "end": v(-13361.42, 13720) * mm});
            skLineSegment(sketch, "E290", {"start": v(-13361.42, 13720) * mm, "end": v(-13657.42, 13720) * mm});
            skLineSegment(sketch, "E291", {"start": v(-13657.42, 13720) * mm, "end": v(-13659.42, 13718) * mm});
            skLineSegment(sketch, "E292", {"start": v(-13659.42, 13718) * mm, "end": v(-13759.42, 13718) * mm});
            skLineSegment(sketch, "E293", {"start": v(-13759.42, 13718) * mm, "end": v(-13761.42, 13720) * mm});
            skLineSegment(sketch, "E294", {"start": v(-13761.42, 13720) * mm, "end": v(-14057.42, 13720) * mm});
            skLineSegment(sketch, "E295", {"start": v(-14057.42, 13720) * mm, "end": v(-14059.42, 13718) * mm});
            skLineSegment(sketch, "E296", {"start": v(-14059.42, 13718) * mm, "end": v(-14159.42, 13718) * mm});
            skLineSegment(sketch, "E297", {"start": v(-14159.42, 13718) * mm, "end": v(-14161.42, 13720) * mm});
            skLineSegment(sketch, "E298", {"start": v(-14161.42, 13720) * mm, "end": v(-14457.42, 13720) * mm});
            skLineSegment(sketch, "E299", {"start": v(-14457.42, 13720) * mm, "end": v(-14459.42, 13718) * mm});
            skLineSegment(sketch, "E300", {"start": v(-14459.42, 13718) * mm, "end": v(-14559.42, 13718) * mm});
            skLineSegment(sketch, "E301", {"start": v(-14559.42, 13718) * mm, "end": v(-14561.42, 13720) * mm});
            skLineSegment(sketch, "E302", {"start": v(-14561.42, 13720) * mm, "end": v(-14761.42, 13720) * mm});
            skLineSegment(sketch, "E303", {"start": v(-14761.42, 3118) * mm, "end": v(-14761.42, -5870) * mm});
            skLineSegment(sketch, "E304", {"start": v(12438.58, -1470) * mm, "end": v(12438.58, 11720) * mm});
            skLineSegment(sketch, "E305", {"start": v(-14761.42, 13720) * mm, "end": v(-14761.42, 4818) * mm});
            skLineSegment(sketch, "E306", {"start": v(-14761.42, 4818) * mm, "end": v(-14761.42, 3118) * mm});
            skLineSegment(sketch, "E307", {"start": v(-11.42, -6370) * mm, "end": v(-11.42, -5870) * mm});
            skLineSegment(sketch, "E308", {"start": v(-511.42, -6370) * mm, "end": v(-11.42, -6370) * mm});
            skLineSegment(sketch, "E309", {"start": v(-511.42, -5870) * mm, "end": v(-511.42, -6370) * mm});
            skLineSegment(sketch, "E310", {"start": v(-11.42, -5870) * mm, "end": v(-511.42, -5870) * mm});
            skLineSegment(sketch, "E311", {"start": v(-7211.42, -6370) * mm, "end": v(-7211.42, -5870) * mm});
            skLineSegment(sketch, "E312", {"start": v(-7711.42, -6370) * mm, "end": v(-7211.42, -6370) * mm});
            skLineSegment(sketch, "E313", {"start": v(-7711.42, -5870) * mm, "end": v(-7711.42, -6370) * mm});
            skLineSegment(sketch, "E314", {"start": v(-7211.42, -5870) * mm, "end": v(-7711.42, -5870) * mm});
            skLineSegment(sketch, "E315", {"start": v(-14761.42, 6695.46) * mm, "end": v(-13431.42, 6695.46) * mm});
            skLineSegment(sketch, "E316", {"start": v(-13431.42, 6695.46) * mm, "end": v(-13431.42, -5070) * mm});
            skLineSegment(sketch, "E317", {"start": v(-13431.42, -5070) * mm, "end": v(-3861.42, -5070) * mm});
            skLineSegment(sketch, "E318", {"start": v(-3861.42, -5070) * mm, "end": v(-3861.42, -720) * mm});
            skLineSegment(sketch, "E319", {"start": v(-3861.42, -720) * mm, "end": v(4138.58, -720) * mm});
            skLineSegment(sketch, "E320", {"start": v(4138.58, -720) * mm, "end": v(4138.58, -1320) * mm});
            skLineSegment(sketch, "E321", {"start": v(4138.58, -1320) * mm, "end": v(9138.58, -1320) * mm});
            skLineSegment(sketch, "E322", {"start": v(9138.58, -1320) * mm, "end": v(9138.58, 6080) * mm});
            skLineSegment(sketch, "E323", {"start": v(-14761.42, -5870) * mm, "end": v(-3161.42, -5870) * mm});
            skLineSegment(sketch, "E324", {"start": v(-3161.42, -5870) * mm, "end": v(-3161.42, -1420) * mm});
            skLineSegment(sketch, "E325", {"start": v(-3161.42, -1420) * mm, "end": v(3438.58, -1420) * mm});
            skLineSegment(sketch, "E326", {"start": v(3438.58, -1420) * mm, "end": v(3438.58, -2520) * mm});
            skLineSegment(sketch, "E327", {"start": v(3438.58, -2520) * mm, "end": v(10338.58, -2520) * mm});
            skLineSegment(sketch, "E328", {"start": v(10338.58, -2520) * mm, "end": v(10338.58, 6080) * mm});
            skLineSegment(sketch, "E329", {"start": v(9138.58, 6080) * mm, "end": v(10338.58, 6080) * mm});
            skLineSegment(sketch, "E330", {"start": v(-14761.42, 4945.46) * mm, "end": v(-13911.42, 4945.46) * mm});
            skArc(sketch, "E331", {"start": v(-13911.42, 4945.46) * mm, "mid": v(-14160.38, 5546.5) * mm, "end": v(-14761.42, 5795.46) * mm});
            skArc(sketch, "E332", {"start": v(-14761.42, 5795.46) * mm, "mid": v(-14125.03, 6059.07) * mm, "end": v(-13861.42, 6695.46) * mm});
            skLineSegment(sketch, "E333", {"start": v(12438.58, -1670) * mm, "end": v(10338.58, -1670) * mm});
            skLineSegment(sketch, "E334", {"start": v(-7711.42, -6370) * mm, "end": v(-7711.42, -13304.54) * mm});
            skLineSegment(sketch, "E335", {"start": v(-10588.42, -5870) * mm, "end": v(-10588.42, -13304.54) * mm});
            skLineSegment(sketch, "E336", {"start": v(-3161.42, -5870) * mm, "end": v(5038.58, -5870) * mm});
            skLineSegment(sketch, "E337", {"start": v(3438.58, -2520) * mm, "end": v(3438.58, -5870) * mm});
            skLineSegment(sketch, "E338.bottom", {"start": v(5038.58, -5870) * mm, "end": v(5538.58, -5870) * mm});
            skLineSegment(sketch, "E338.top", {"start": v(5038.58, -6370) * mm, "end": v(5538.58, -6370) * mm});
            skLineSegment(sketch, "E338.left", {"start": v(5038.58, -5870) * mm, "end": v(5038.58, -6370) * mm});
            skLineSegment(sketch, "E338.right", {"start": v(5538.58, -5870) * mm, "end": v(5538.58, -6370) * mm});
            skLineSegment(sketch, "E339.bottom", {"start": v(-511.42, -1420) * mm, "end": v(-11.42, -1420) * mm});
            skLineSegment(sketch, "E339.top", {"start": v(-511.42, -1920) * mm, "end": v(-11.42, -1920) * mm});
            skLineSegment(sketch, "E339.left", {"start": v(-511.42, -1420) * mm, "end": v(-511.42, -1920) * mm});
            skLineSegment(sketch, "E339.right", {"start": v(-11.42, -1420) * mm, "end": v(-11.42, -1920) * mm});
            skLineSegment(sketch, "E340", {"start": v(12438.58, 12120) * mm, "end": v(12438.58, 13720) * mm});
            skSolve(sketch);
        }
        {
            var Q0;
            Q0=qCreatedBy(makeId("Top.planeOp"),FACE);
            var sketch = newSketch(context, id + "F1", { "sketchPlane" : qUnion([Q0])});
            skLineSegment(sketch, "E341", {"start": v(-3861.42, -5070) * mm, "end": v(-3861.42, 3280) * mm});
            skLineSegment(sketch, "E342", {"start": v(-9286.42, -5070) * mm, "end": v(-9286.42, 930) * mm, "construction": true});
            skLineSegment(sketch, "E343", {"start": v(-11986.42, -5070) * mm, "end": v(-11986.42, 930) * mm});
            skLineSegment(sketch, "E344", {"start": v(10338.58, 11730) * mm, "end": v(10338.58, 8930) * mm});
            skLineSegment(sketch, "E345", {"start": v(10338.58, 8930) * mm, "end": v(7238.58, 8930) * mm});
            skLineSegment(sketch, "E346", {"start": v(7238.58, 8930) * mm, "end": v(7238.58, 11730) * mm});
            skLineSegment(sketch, "E347", {"start": v(7238.58, 11730) * mm, "end": v(10338.58, 11730) * mm});
            skLineSegment(sketch, "E348", {"start": v(-6586.42, -5070) * mm, "end": v(-3861.42, -5070) * mm});
            skLineSegment(sketch, "E349", {"start": v(-9286.42, 930) * mm, "end": v(-9261.42, 930) * mm});
            skLineSegment(sketch, "E350", {"start": v(-11986.42, 930) * mm, "end": v(-11936.42, 930) * mm});
            skLineSegment(sketch, "E351", {"start": v(-9286.42, -5070) * mm, "end": v(-6586.42, -5070) * mm});
            skLineSegment(sketch, "E352", {"start": v(-11986.42, -5070) * mm, "end": v(-9286.42, -5070) * mm});
            skLineSegment(sketch, "E353", {"start": v(-3911.42, 3280) * mm, "end": v(-3911.42, -5020) * mm});
            skLineSegment(sketch, "E354", {"start": v(-3911.42, -5020) * mm, "end": v(-6561.42, -5020) * mm});
            skLineSegment(sketch, "E355", {"start": v(-6561.42, -5020) * mm, "end": v(-6561.42, -1020) * mm});
            skLineSegment(sketch, "E356.trimOffspring", {"start": v(-3911.42, 3280) * mm, "end": v(-3861.42, 3280) * mm});
            skLineSegment(sketch, "E357", {"start": v(-6611.42, -1020) * mm, "end": v(-6611.42, -5020) * mm});
            skLineSegment(sketch, "E358", {"start": v(-6611.42, -5020) * mm, "end": v(-9261.42, -5020) * mm});
            skLineSegment(sketch, "E359", {"start": v(-9261.42, -5020) * mm, "end": v(-9261.42, 930) * mm});
            skLineSegment(sketch, "E360", {"start": v(-6611.42, -1020) * mm, "end": v(-6561.42, -1020) * mm});
            skLineSegment(sketch, "E361", {"start": v(-6586.42, -1020) * mm, "end": v(-6586.42, -5070) * mm, "construction": true});
            skLineSegment(sketch, "E362", {"start": v(-9311.42, 930) * mm, "end": v(-9311.42, -5020) * mm});
            skLineSegment(sketch, "E363", {"start": v(-9311.42, -5020) * mm, "end": v(-11936.42, -5020) * mm});
            skLineSegment(sketch, "E364", {"start": v(-11936.42, -5020) * mm, "end": v(-11936.42, 930) * mm});
            skLineSegment(sketch, "E365.trimOffspring", {"start": v(-9311.42, 930) * mm, "end": v(-9286.42, 930) * mm});
            skLineSegment(sketch, "E366", {"start": v(-3886.42, 3280) * mm, "end": v(-3886.42, -5070) * mm, "construction": true});
            skLineSegment(sketch, "E367", {"start": v(-1186.42, 3280) * mm, "end": v(-1186.42, -720) * mm, "construction": true});
            skLineSegment(sketch, "E368", {"start": v(-1186.42, -720) * mm, "end": v(-3861.42, -720) * mm});
            skLineSegment(sketch, "E369", {"start": v(-3861.42, -670) * mm, "end": v(-1211.42, -670) * mm});
            skLineSegment(sketch, "E370", {"start": v(-1211.42, -670) * mm, "end": v(-1211.42, 3330) * mm});
            skLineSegment(sketch, "E371", {"start": v(-1161.42, 3330) * mm, "end": v(-1161.42, -670) * mm});
            skLineSegment(sketch, "E372", {"start": v(-1161.42, -670) * mm, "end": v(1438.58, -670) * mm});
            skLineSegment(sketch, "E373", {"start": v(1438.58, -670) * mm, "end": v(1438.58, 3330) * mm});
            skLineSegment(sketch, "E374", {"start": v(1438.58, 3330) * mm, "end": v(1488.58, 3330) * mm});
            skLineSegment(sketch, "E375", {"start": v(1488.58, 3330) * mm, "end": v(1488.58, -720) * mm});
            skLineSegment(sketch, "E376", {"start": v(1488.58, -720) * mm, "end": v(-1186.42, -720) * mm});
            skLineSegment(sketch, "E377", {"start": v(-1161.42, 3330) * mm, "end": v(-1211.42, 3330) * mm});
            skLineSegment(sketch, "E378.bottom", {"start": v(-14761.42, 13720) * mm, "end": v(7238.58, 13720) * mm});
            skLineSegment(sketch, "E378.top", {"start": v(-14761.42, 8220) * mm, "end": v(7238.58, 8220) * mm});
            skLineSegment(sketch, "E378.left", {"start": v(-14761.42, 13720) * mm, "end": v(-14761.42, 8220) * mm});
            skLineSegment(sketch, "E378.right", {"start": v(7238.58, 13720) * mm, "end": v(7238.58, 8220) * mm});
            skLineSegment(sketch, "E379", {"start": v(7238.58, 11730) * mm, "end": v(7238.58, 8930) * mm});
            skLineSegment(sketch, "E380.bottom", {"start": v(10068.58, 13720) * mm, "end": v(11268.58, 13720) * mm});
            skLineSegment(sketch, "E380.top", {"start": v(10068.58, 12085) * mm, "end": v(11268.58, 12085) * mm});
            skLineSegment(sketch, "E380.left", {"start": v(10068.58, 13720) * mm, "end": v(10068.58, 12085) * mm});
            skLineSegment(sketch, "E380.right", {"start": v(11268.58, 13720) * mm, "end": v(11268.58, 12085) * mm});
            skLineSegment(sketch, "E381.bottom", {"start": v(7431.92, 13398.08) * mm, "end": v(9831.92, 13398.08) * mm});
            skLineSegment(sketch, "E381.top", {"start": v(7431.92, 12198.08) * mm, "end": v(9831.92, 12198.08) * mm});
            skLineSegment(sketch, "E381.left", {"start": v(7431.92, 13398.08) * mm, "end": v(7431.92, 12198.08) * mm});
            skLineSegment(sketch, "E381.right", {"start": v(9831.92, 13398.08) * mm, "end": v(9831.92, 12198.08) * mm});
            skLineSegment(sketch, "E382", {"start": v(4138.58, 3330) * mm, "end": v(4138.58, -720) * mm});
            skLineSegment(sketch, "E383", {"start": v(1488.58, -720) * mm, "end": v(4138.58, -720) * mm});
            skLineSegment(sketch, "E384", {"start": v(4138.58, 3330) * mm, "end": v(4088.58, 3330) * mm});
            skLineSegment(sketch, "E385", {"start": v(4088.58, 3330) * mm, "end": v(4088.58, -670) * mm});
            skLineSegment(sketch, "E386", {"start": v(4088.58, -670) * mm, "end": v(1488.58, -670) * mm});
            skSolve(sketch);
        }
        {
            var Q0;
            Q0=makeQuery(id+"F0.imprint","IMPRINT",FACE,{"disambiguationData":[TD([[makeQuery(id+"F0.imprint","IMPRINT",EDGE,{"derivedFrom":sQuery(id+"F0.wireOp",EDGE,"E0")}),-1.0]])]});
            extrude(context, id + "F2", {"entities" : qUnion([Q0]), "depth" : 25 * mm, "offsetDistance" : 25 * mm});
        }
        {
            var Q0;
            {var subQ10=sQuery(id+"F0.wireOp",EDGE,"E303");Q0=makeQuery(id+"F0.imprint","IMPRINT",FACE,{"disambiguationData":[TD([[makeQuery(id+"F0.imprint","IMPRINT",EDGE,{"derivedFrom":subQ10}),1.0]])]});}
            var Q1;
            {var subQ0=sQuery(id+"F0.wireOp",EDGE,"E330");Q1=makeQuery(id+"F0.imprint","IMPRINT",FACE,{"disambiguationData":[TD([[makeQuery(id+"F0.imprint","IMPRINT",EDGE,{"derivedFrom":subQ0}),1.0]])]});}
            var Q2;
            {var subQ3=sQuery(id+"F0.wireOp",EDGE,"E332");Q2=makeQuery(id+"F0.imprint","IMPRINT",FACE,{"disambiguationData":[TD([[makeQuery(id+"F0.imprint","IMPRINT",EDGE,{"derivedFrom":subQ3}),1.0]])]});}
            extrude(context, id + "F3", {"entities" : qUnion([Q0, Q1, Q2]), "depth" : 25 * mm, "offsetDistance" : 25 * mm});
        }
        {
            var Q0;
            {var subQ0=sQuery(id+"F0.wireOp",EDGE,"E311");Q0=makeQuery(id+"F0.imprint","IMPRINT",FACE,{"disambiguationData":[TD([[makeQuery(id+"F0.imprint","IMPRINT",EDGE,{"derivedFrom":subQ0}),1.0]])]});}
            var Q1;
            Q1=makeQuery(id+"F0.imprint","IMPRINT",FACE,{"disambiguationData":[TD([[makeQuery(id+"F0.imprint","IMPRINT",EDGE,{"derivedFrom":sQuery(id+"F0.wireOp",EDGE,"E307")}),1.0]])]});
            var Q2;
            Q2=makeQuery(id+"F0.imprint","IMPRINT",FACE,{"disambiguationData":[TD([[makeQuery(id+"F0.imprint","IMPRINT",EDGE,{"derivedFrom":sQuery(id+"F0.wireOp",EDGE,"E339.bottom")}),-1.0]])]});
            var Q3;
            Q3=makeQuery(id+"F0.imprint","IMPRINT",FACE,{"disambiguationData":[TD([[makeQuery(id+"F0.imprint","IMPRINT",EDGE,{"derivedFrom":sQuery(id+"F0.wireOp",EDGE,"E338.bottom")}),-1.0]])]});
            extrude(context, id + "F4", {"entities" : qUnion([Q0, Q1, Q2, Q3]), "depth" : 25 * mm, "offsetDistance" : 25 * mm});
        }
        {
            var Q0;
            Q0=makeQuery(id+"F1.imprint","IMPRINT",FACE,{"disambiguationData":[TD([[makeQuery(id+"F1.imprint","IMPRINT",EDGE,{"derivedFrom":sQuery(id+"F1.wireOp",EDGE,"E344")}),-1.0]])]});
            extrude(context, id + "F5", {"entities" : qUnion([Q0]), "depth" : 26 * mm, "offsetDistance" : 25 * mm, "hasSecondDirectionOffset" : true, "secondDirectionOffsetDistance" : 25 * mm});
        }
        {
            var Q0;
            {var subQ1=sQuery(id+"F0.wireOp",EDGE,"E11");Q0=makeQuery(id+"F0.imprint","IMPRINT",FACE,{"disambiguationData":[TD([[makeQuery(id+"F0.imprint","IMPRINT",EDGE,{"derivedFrom":subQ1}),1.0]])]});}
            extrude(context, id + "F6", {"entities" : qUnion([Q0]), "depth" : 25 * mm, "offsetDistance" : 25 * mm});
        }
        {
            var Q0;
            Q0=makeQuery(id+"F0.imprint","IMPRINT",FACE,{"disambiguationData":[TD([[makeQuery(id+"F0.imprint","IMPRINT",EDGE,{"derivedFrom":sQuery(id+"F0.wireOp",EDGE,"E3")}),1.0]])]});
            extrude(context, id + "F7", {"entities" : qUnion([Q0]), "depth" : 25 * mm, "offsetDistance" : 25 * mm});
        }
        {
            var Q0;
            Q0=makeQuery(id+"F1.imprint","IMPRINT",FACE,{"disambiguationData":[TD([[makeQuery(id+"F1.imprint","IMPRINT",EDGE,{"derivedFrom":sQuery(id+"F1.wireOp",EDGE,"E343")}),-1.0]])]});
            var Q1;
            {var subQ0=sQuery(id+"F1.wireOp",EDGE,"E368");Q1=makeQuery(id+"F1.imprint","IMPRINT",FACE,{"disambiguationData":[TD([[makeQuery(id+"F1.imprint","IMPRINT",EDGE,{"derivedFrom":subQ0}),-1.0]])]});}
            var Q2;
            Q2=makeQuery(id+"F1.imprint","IMPRINT",FACE,{"disambiguationData":[TD([[makeQuery(id+"F1.imprint","IMPRINT",EDGE,{"derivedFrom":sQuery(id+"F1.wireOp",EDGE,"E382")}),-1.0]])]});
            extrude(context, id + "F8", {"entities" : qUnion([Q0, Q1, Q2]), "depth" : 26 * mm, "offsetDistance" : 25 * mm});
        }
        {
            var Q0;
            {var subQ2=sQuery(id+"F1.wireOp",EDGE,"E378.bottom");Q0=makeQuery(id+"F1.imprint","IMPRINT",FACE,{"disambiguationData":[TD([[makeQuery(id+"F1.imprint","IMPRINT",EDGE,{"derivedFrom":subQ2}),-1.0]])]});}
            extrude(context, id + "F9", {"entities" : qUnion([Q0]), "depth" : 26 * mm, "offsetDistance" : 25 * mm});
        }
        {
            var Q0;
            {var subQ1=sQuery(id+"F0.wireOp",EDGE,"E313");Q0=makeQuery(id+"F0.imprint","IMPRINT",FACE,{"disambiguationData":[TD([[makeQuery(id+"F0.imprint","IMPRINT",EDGE,{"derivedFrom":subQ1}),-1.0]])]});}
            extrude(context, id + "F10", {"entities" : qUnion([Q0]), "depth" : 25 * mm, "offsetDistance" : 25 * mm});
        }
        {
            var Q0;
            {var subQ1=sQuery(id+"F0.wireOp",EDGE,"E13");Q0=makeQuery(id+"F0.imprint","IMPRINT",FACE,{"disambiguationData":[TD([[makeQuery(id+"F0.imprint","IMPRINT",EDGE,{"derivedFrom":subQ1}),1.0]])]});}
            extrude(context, id + "F11", {"entities" : qUnion([Q0]), "depth" : 25 * mm, "offsetDistance" : 25 * mm});
        }
        {
            var Q0;
            {var subQ2=sQuery(id+"F0.wireOp",EDGE,"E324");Q0=makeQuery(id+"F0.imprint","IMPRINT",FACE,{"disambiguationData":[TD([[makeQuery(id+"F0.imprint","IMPRINT",EDGE,{"derivedFrom":subQ2}),-1.0]])]});}
            extrude(context, id + "F12", {"entities" : qUnion([Q0]), "depth" : 25 * mm, "offsetDistance" : 25 * mm});
        }
        {
            var Q0;
            Q0=makeQuery(id+"F0.imprint","IMPRINT",FACE,{"disambiguationData":[TD([[makeQuery(id+"F0.imprint","IMPRINT",EDGE,{"derivedFrom":sQuery(id+"F0.wireOp",EDGE,"E14")}),-1.0]])]});
            extrude(context, id + "F13", {"entities" : qUnion([Q0]), "depth" : 25 * mm, "offsetDistance" : 25 * mm});
        }
        {
            var Q0;
            Q0=makeQuery(id+"F0.imprint","IMPRINT",FACE,{"disambiguationData":[TD([[makeQuery(id+"F0.imprint","IMPRINT",EDGE,{"derivedFrom":sQuery(id+"F0.wireOp",EDGE,"E8")}),1.0]])]});
            extrude(context, id + "F14", {"entities" : qUnion([Q0]), "depth" : 25 * mm, "offsetDistance" : 25 * mm});
        }
        {
            var Q0;
            Q0=makeQuery(id+"F1.imprint","IMPRINT",FACE,{"disambiguationData":[TD([[makeQuery(id+"F1.imprint","IMPRINT",EDGE,{"derivedFrom":sQuery(id+"F1.wireOp",EDGE,"E380.bottom")}),-1.0]])]});
            extrude(context, id + "F15", {"entities" : qUnion([Q0]), "depth" : 26 * mm, "offsetDistance" : 25 * mm});
        }
        {
            var Q0;
            Q0=makeQuery(id+"F1.imprint","IMPRINT",FACE,{"disambiguationData":[TD([[makeQuery(id+"F1.imprint","IMPRINT",EDGE,{"derivedFrom":sQuery(id+"F1.wireOp",EDGE,"E381.bottom")}),-1.0]])]});
            extrude(context, id + "F16", {"entities" : qUnion([Q0]), "depth" : 26 * mm, "offsetDistance" : 25 * mm});
        }
    });
